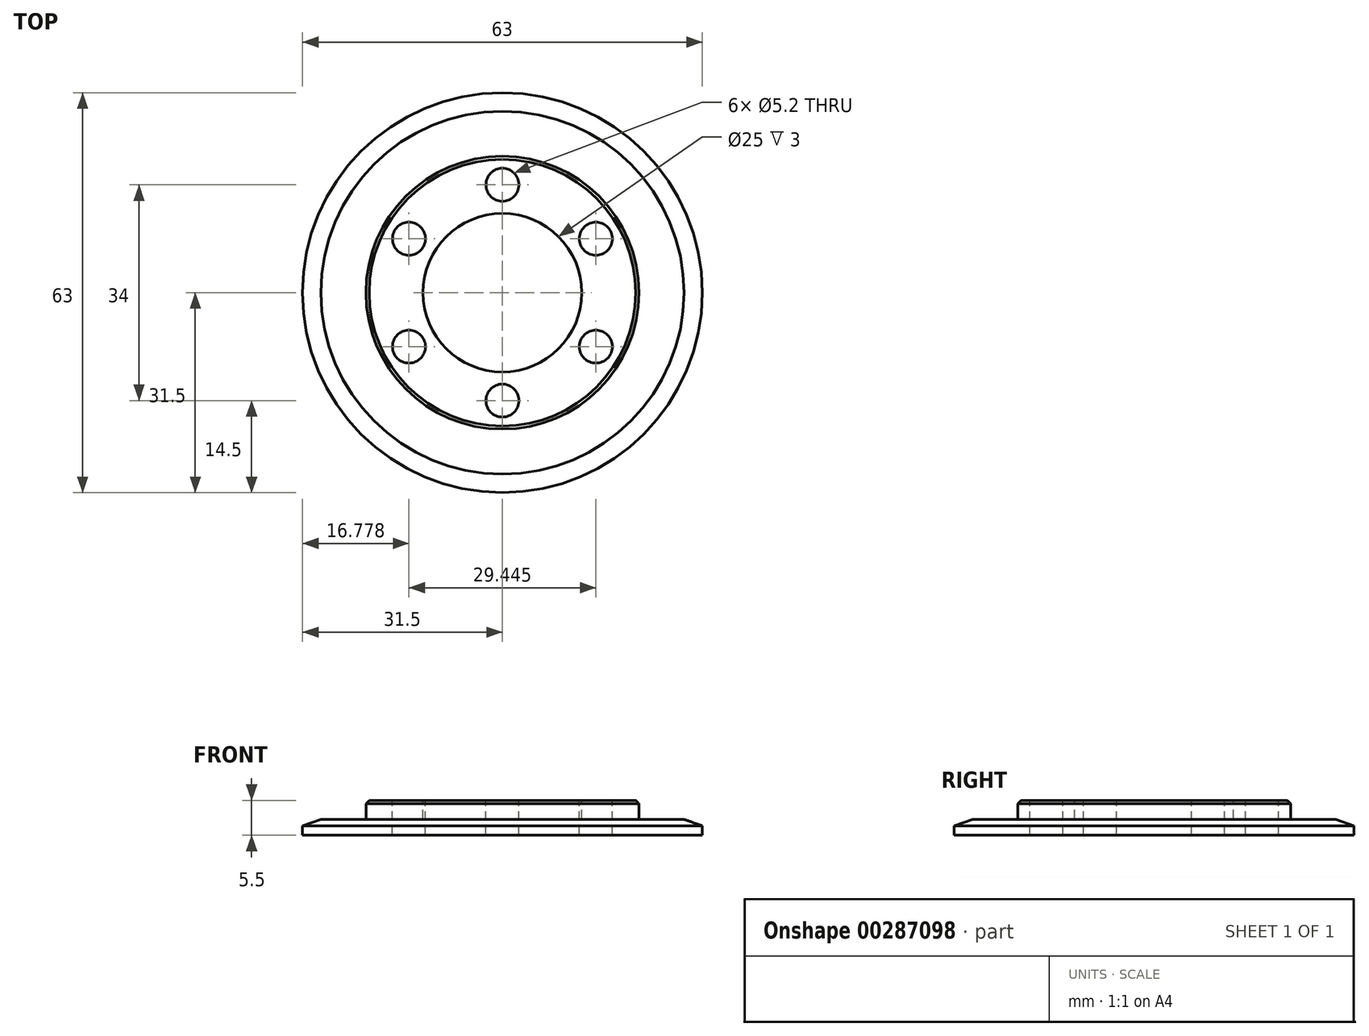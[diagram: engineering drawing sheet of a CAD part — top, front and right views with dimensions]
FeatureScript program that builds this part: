
annotation { "Feature Type Name" : "Feature", "Feature Type Description" : "" }
export const myFeature = defineFeature(function(context is Context, id is Id, definition is map)
    precondition{}
    {
        {
            var Q0;
            Q0=qCreatedBy(makeId("Top.planeOp"),FACE);
            var sketch = newSketch(context, id + "F0", { "sketchPlane" : qUnion([Q0])});
            skCircle(sketch, "E0", {"center": v(0, 0) * mm, "radius": 31.5 * mm});
            skSolve(sketch);
        }
        {
            var Q0;
            Q0 = qSketchRegion(id + "F0", true);
            extrude(context, id + "F1", {"entities" : qUnion([Q0]), "depth" : 2.5 * mm});
        }
        {
            var Q0;
            Q0=makeQuery(id+"F1.opExtrude","CAP_FACE",FACE,{"disambiguationData":[OSD([sQuery(id+"F0.wireOp",EDGE,"E0")])],"isStart":false});
            var sketch = newSketch(context, id + "F2", { "sketchPlane" : qUnion([Q0])});
            skCircle(sketch, "E1", {"center": v(0, 0) * mm, "radius": 21.5 * mm});
            skSolve(sketch);
        }
        {
            var Q0;
            Q0 = qSketchRegion(id + "F2", true);
            extrude(context, id + "F3", {"entities" : qUnion([Q0]), "operationType" : NewBodyOperationType.ADD, "depth" : 3 * mm});
        }
        {
            var Q0;
            Q0=makeQuery(id+"F1.opExtrude","CAP_EDGE",EDGE,{"disambiguationData":[OSD([sQuery(id+"F0.wireOp",EDGE,"E0")])],"isStart":false});
            chamfer(context, id + "F4", {"entities" : qUnion([Q0]), "chamferType" : ChamferType.TWO_OFFSETS, "width1" : 2.9 * mm, "oppositeDirection" : false, "width2" : 1 * mm, "tangentPropagation" : true});
        }
        {
            var Q0;
            Q0=makeQuery(id+"F3.opExtrude","CAP_FACE",FACE,{"disambiguationData":[OSD([sQuery(id+"F2.wireOp",EDGE,"E1")])],"isStart":false});
            var sketch = newSketch(context, id + "F5", { "sketchPlane" : qUnion([Q0])});
            skCircle(sketch, "E2", {"center": v(0, 0) * mm, "radius": 17 * mm, "construction": true});
            skPoint(sketch, "E3", {"position": v(0, 17) * mm});
            skCircle(sketch, "E4", {"center": v(0, 17) * mm, "radius": 2.6 * mm});
            skSolve(sketch);
        }
        {
            var Q0;
            Q0 = qSketchRegion(id + "F5", true);
            extrude(context, id + "F6", {"entities" : qUnion([Q0]), "operationType" : NewBodyOperationType.REMOVE, "endBound" : BoundingType.UP_TO_NEXT, "oppositeDirection" : true, "depth" : 25 * mm});
        }
        {
            var Q0;
            Q0=makeQuery(id+"F3.opExtrude","CAP_FACE",FACE,{"disambiguationData":[OSD([sQuery(id+"F2.wireOp",EDGE,"E1")])],"isStart":false});
            var sketch = newSketch(context, id + "F7", { "sketchPlane" : qUnion([Q0])});
            skCircle(sketch, "E5", {"center": v(0, 0) * mm, "radius": 12.5 * mm});
            skSolve(sketch);
        }
        {
            var Q0;
            Q0=makeQuery(id+"F1.opExtrude","SWEPT_BODY",BODY,{"disambiguationData":[OSD([sQuery(id+"F0.wireOp",EDGE,"E0")])]});
            var Q1;
            Q1=makeQuery(id+"F6.boolean.opBoolean","COPY",FACE,{"derivedFrom":makeQuery(id+"F6.opExtrude","SWEPT_FACE",FACE,{"disambiguationData":[OSD([sQuery(id+"F5.wireOp",EDGE,"E4")])]})});
            var Q2;
            Q2=sQuery(id+"F7.wireOp",EDGE,"E5");
            circularPattern(context, id + "F8", {"patternType" : PatternType.FACE, "faces" : qUnion([Q1]), "axis" : qUnion([Q2]), "angle" : 360 * degree, "instanceCount" : 6, "equalSpace" : true});
        }
        {
            var Q0;
            Q0 = qSketchRegion(id + "F7", true);
            extrude(context, id + "F9", {"entities" : qUnion([Q0]), "operationType" : NewBodyOperationType.REMOVE, "oppositeDirection" : true, "depth" : 3 * mm});
        }
        {
            var Q0;
            Q0=makeQuery(id+"F3.opExtrude","CAP_EDGE",EDGE,{"disambiguationData":[OSD([sQuery(id+"F2.wireOp",EDGE,"E1")])],"isStart":false});
            chamfer(context, id + "F10", {"entities" : qUnion([Q0]), "width" : 0.5 * mm, "tangentPropagation" : true});
        }
    });
